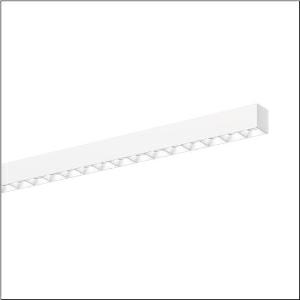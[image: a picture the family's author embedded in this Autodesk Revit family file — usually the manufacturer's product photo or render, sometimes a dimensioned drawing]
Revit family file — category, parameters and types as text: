
# Revit family: silica_r__21_51mx26dc4awb_5f84
name_source: partatom
category: Lighting Fixtures
units: mm (PartAtom-declared; Revit-internal decimal feet)

## family parameters
Cut with Voids When Loaded = No
Host = Face
Light Source = No
Part Type = Normal
Room Calculation Point = No
Round Connector Dimension = Use Diameter
Shared = No

## types (1)
- --- (1 x LED, 10800 lm, 60.6 W, 4000K)
    Apparent Load = 61 VA
    CIE Flux Codes = 83 98 100 100 100
    Color Rendering = 80
    Color Temperature = 4000K
    Default Elevation = 1800 mm
    Description = Silica® 21, office luminaire, primary light control with darklight reflector, of PMMA, white, CAT 2 (L<= 3000cd/m²), light emission: direct distribution, primary light characteristic: symmetric, installation type: surface-mounted, LED, rated luminous flux: 10.800lm, luminous efficacy: 178lm/W, light colour: 840, colour temperature: 4000K, with terminal, 3+2-pole, max. 2.5mm², mains connection: 220..240V, AC, 50/60Hz, rated input power: 60.6W, luminaire housing, of aluminium, traffic white (RAL 9016), length: 3.004mm, width: 53mm, height: 53mm, protection rating (complete): IP20, insulation class (complete): insulation class I (protective earthing), certification: CE, permissible operating ambient temperature: 0..+35°C, standard: EN 50419, packaging unit: 1 piece
    Height = 0 mm  [stored 0 ft]
    Lamp = 1 x LED
    Lamp Light Flux = 10800 lm
    Lamp Power = 60.6 W
    Lamp count = 1
    Length = 3004 mm
    Luminous efficacy = 178 lm/W
    Manufacturer = Siteco
    ModVariant = No
    Model = 51MX26DC4AWB
    Mounting Place = Ceiling
    Mounting Type = Recessed
    Number of Poles = 1
    OnlyDefault = Yes
    Power Factor = 1
    Product Name = Silica® 21
    Product group = office luminaire | ceiling recessed
    ProductGroupID = 401
    Protection Class = Protection class I
    Protection Degree = IP 20
    RLX_Detail_Level = 1
    RLX_Emergency_Light_Flux = 0 lm
    RLX_Emergency_Type = 0
    RLX_Emergency_Type_DB = No
    RlxData = <blob elided: 59653 chars, md5=1302af9d>
    Socket = socket
    Standby Power = 0 W
    System Light Flux = 10800 lm
    System Power = 61 W
    Type Comments = factory setting: luminous flux: 100 % | dim-lin: 254 | 336 mA
    Type Image = l_1313597.jpg
    URL = http://relux.com
    VarID = @adj_073483
    Voltage = 0 V
    Weight = 0.00 kg
    Width = 53 mm

note: [stored X ft] marks values corroborated as IEEE doubles in the binary element streams (Revit-internal decimal feet)

## geometry (parser evidence)
native form markers: Blend x4, Sweep x11
no freeform markers — native parametric forms only
